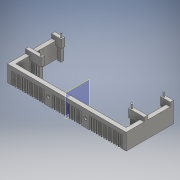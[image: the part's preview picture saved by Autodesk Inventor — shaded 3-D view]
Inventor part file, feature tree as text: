
AUTODESK INVENTOR PART (.ipt)
format: ipt  version: 2016 SP2 (Build 200236200, 236)  size: 636,928 bytes
history: native  units: mm
features: extrude x18, sketch x18, mirror x7, other x1
ambient origin geometry x8: Origin, YZ Plane, XZ Plane, XY Plane, X Axis, Y Axis, Z Axis, Center Point
bodies: Solid1 (feature_tree)
feature tree (44):
  extrude  "Frame"  Depth=4.0mm
  extrude  "Pins"  Depth=4.0mm
  extrude  "Connection Points"  Depth=17.0mm
  extrude  "Nail Holes"  Depth=5.0mm
  extrude  "Legs"  Depth=5.0mm
  extrude  "Lower Rim 1"  Depth=5.0mm TaperAngle=0.0deg
  other  "Midplane vertical"
  mirror  "Lower Rim Mirror 1"
  extrude  "Supports Peg"  Depth=2.0mm
  extrude  "Nail Heads"  Depth=35.5mm
  extrude  "Supports Front"  Depth=5.0mm
  mirror  "Mirror3"
  extrude  "Internal Supports Front"  Depth=5.0mm
  mirror  "Mirror4"
  extrude  "Side Frame Extension"  Depth=15.0mm TaperAngle=0.0deg
  extrude  "Back Bar"  Depth=10.0mm TaperAngle=0.0deg
  mirror  "Between two Rows"
  extrude  "BoxRest"  Depth=4.0mm
  mirror  "Mirror6"
  extrude  "Front peg bottoms"  Depth=6.0mm
  extrude  "Front peg tops"  Depth=3.0mm TaperAngle=0.0deg
  mirror  "Mirror7"
  extrude  "Front Supports"  Depth=1.0mm
  mirror  "Mirror8"
  extrude  "Resizing"  Depth=1.0mm
  extrude  "Robust peg bottoms"  Depth=1.0mm
  sketch  "Sketch1"  dims[d0=4.0mm d1=4.0mm]
  sketch  "Sketch2"  dims[d2=4.0mm d3=4.0mm]
  sketch  "Sketch3"  dims[d4=17.0mm d5=17.0mm]
  sketch  "Sketch4"  dims[d6=111.2mm d7=5.0mm]
  sketch  "Sketch6"  dims[d8=5.0mm d9=5.0mm]
  sketch  "Sketch8"  dims[d10=10.0mm d11=5.0mm d12=0.0mm]
  sketch  "Sketch11"  dims[d13=4.0mm d14=2.0mm]
  sketch  "Sketch12"  dims[d15=10.0mm d16=0.0mm d17=35.5mm]
  sketch  "Sketch13"  dims[d18=10.0mm d19=5.0mm]
  sketch  "Sketch14"  dims[d20=15.0mm d21=0.0mm d22=5.0mm]
  sketch  "Sketch15"  dims[d23=4.0mm d24=15.0mm d25=0.0mm]
  sketch  "Sketch16"  dims[d29=15.0mm d30=0.0mm d41=10.0mm d42=0.0mm]
  sketch  "Sketch17"  dims[d47=1.0mm d48=2.0mm d49=1.0mm d50=2.0mm d51=1.0mm d52=2.0mm d53=1.0mm d54=2.0mm d55=4.0mm]
  sketch  "Sketch18"  dims[d56=15.0mm d57=0.0mm d58=6.0mm]
  sketch  "Sketch19"  dims[d59=6.0mm d60=3.0mm d61=0.0mm]
  sketch  "Sketch20"  dims[d62=2.0mm d63=1.0mm]
  sketch  "Sketch21"  dims[d64=3.0mm d65=1.0mm]
  sketch  "Sketch22"  dims[d66=2.0mm d67=1.0mm d68=2.0mm d69=1.0mm d70=2.0mm d71=1.0mm d72=2.0mm d73=1.0mm d74=2.0mm d75=1.0mm d76=2.0mm d77=1.0mm d78=2.0mm d79=1.0mm d80=2.0mm d81=1.0mm d82=2.0mm d83=1.0mm d84=2.0mm d85=1.0mm d86=2.0mm d87=1.0mm d88=15.0mm d89=0.0mm d90=2.0mm d91=1.0mm d92=5.0mm d93=2.0mm d94=1.0mm d95=2.0mm d96=1.0mm d97=2.0mm d98=1.0mm d99=2.0mm d100=1.0mm d101=2.0mm d102=15.0mm d103=0.0mm d104=40.0mm d105=0.0mm d106=5.0mm d107=4.0mm d108=31.928mm d109=7.0mm d110=0.0mm d111=4.0mm d112=5.0mm d113=0.0mm d114=4.0mm d115=4.0mm d116=125.53mm d117=5.0mm d118=0.0mm d119=2.0mm d120=5.0mm d121=0.0mm d122=4.0mm d123=2.0mm d124=1.0mm d125=2.0mm d126=1.0mm d127=15.0mm d128=0.0mm d129=8.072mm d130=0.0mm d131=5.0mm d132=0.0mm]
